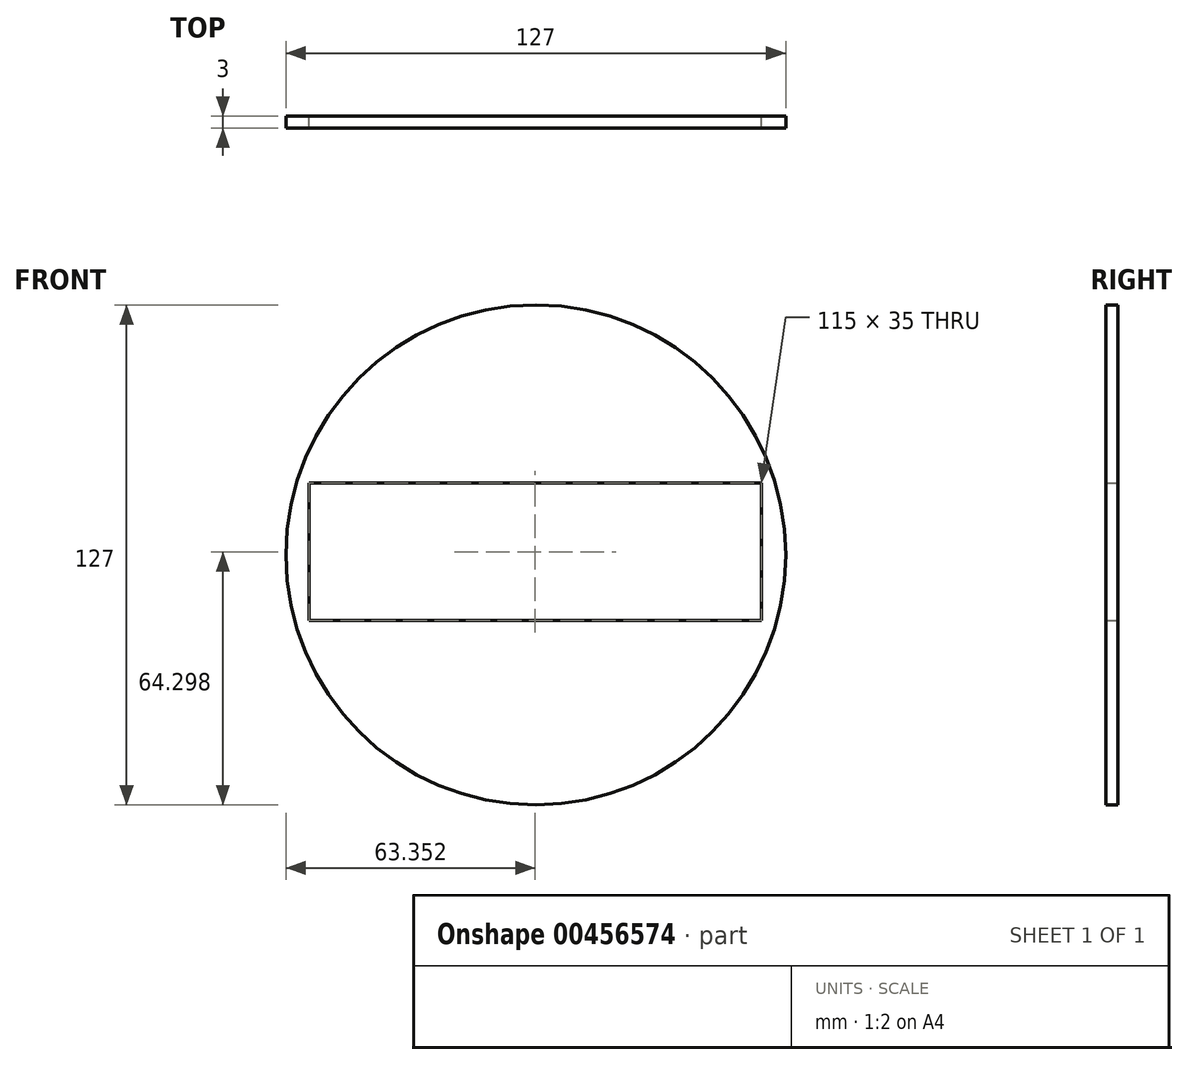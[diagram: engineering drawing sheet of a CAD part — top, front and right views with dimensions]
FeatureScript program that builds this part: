
annotation { "Feature Type Name" : "Feature", "Feature Type Description" : "" }
export const myFeature = defineFeature(function(context is Context, id is Id, definition is map)
    precondition{}
    {
        {
            var Q0;
            Q0=qCreatedBy(makeId("Front.planeOp"),FACE);
            var sketch = newSketch(context, id + "F0", { "sketchPlane" : qUnion([Q0])});
            skCircle(sketch, "E0", {"center": v(0, 0) * mm, "radius": 63.5 * mm});
            skSolve(sketch);
        }
        {
            var Q0;
            Q0 = qSketchRegion(id + "F0", true);
            extrude(context, id + "F1", {"entities" : qUnion([Q0]), "depth" : 3 * mm});
        }
        {
            var Q0;
            Q0=qCreatedBy(makeId("Front.planeOp"),FACE);
            var sketch = newSketch(context, id + "F2", { "sketchPlane" : qUnion([Q0])});
            skLineSegment(sketch, "E1.bottom", {"start": v(-57.65, 18.3) * mm, "end": v(57.35, 18.3) * mm});
            skLineSegment(sketch, "E1.top", {"start": v(-57.65, -16.7) * mm, "end": v(57.35, -16.7) * mm});
            skLineSegment(sketch, "E1.left", {"start": v(-57.65, 18.3) * mm, "end": v(-57.65, -16.7) * mm});
            skLineSegment(sketch, "E1.right", {"start": v(57.35, 18.3) * mm, "end": v(57.35, -16.7) * mm});
            skSolve(sketch);
        }
        {
            var Q0;
            Q0 = qSketchRegion(id + "F2", true);
            extrude(context, id + "F3", {"entities" : qUnion([Q0]), "operationType" : NewBodyOperationType.REMOVE, "depth" : 3 * mm});
        }
    });
